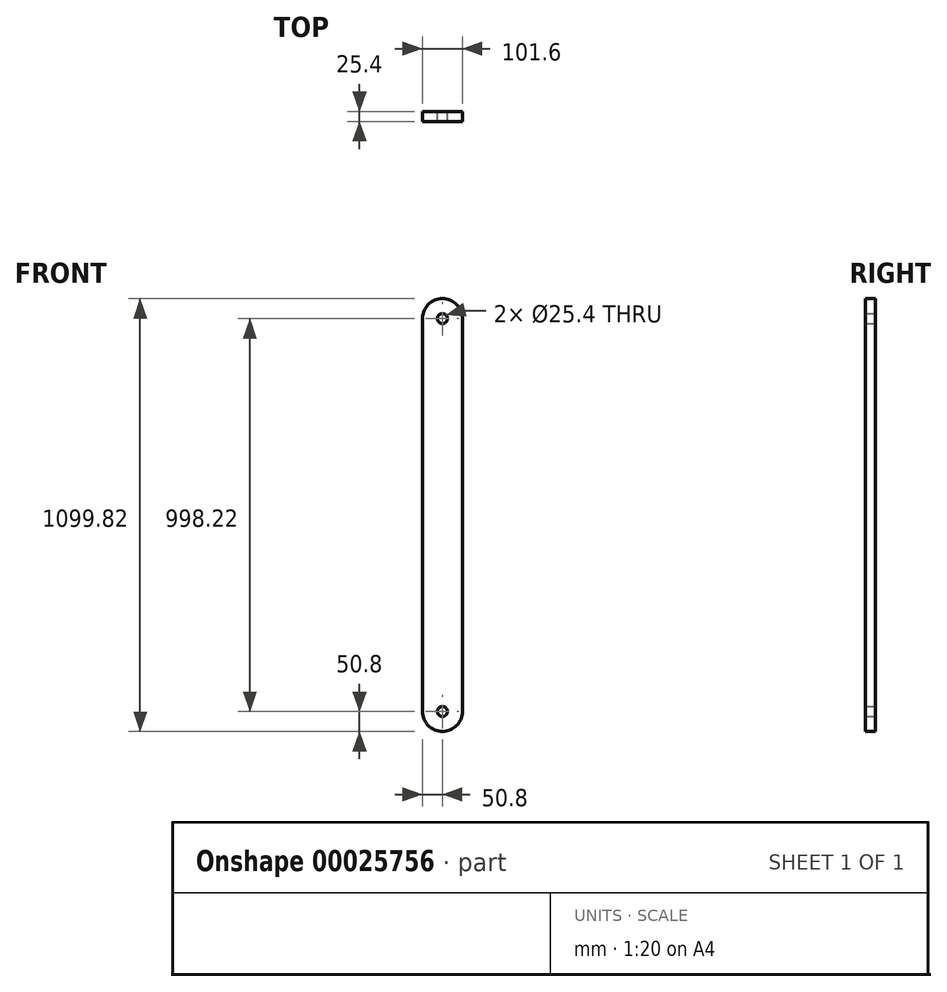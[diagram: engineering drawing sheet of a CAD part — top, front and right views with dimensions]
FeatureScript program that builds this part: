
annotation { "Feature Type Name" : "Feature", "Feature Type Description" : "" }
export const myFeature = defineFeature(function(context is Context, id is Id, definition is map)
    precondition{}
    {
        {
            var Q0;
            Q0=qCreatedBy(makeId("Front.planeOp"),FACE);
            var sketch = newSketch(context, id + "F0", { "sketchPlane" : qUnion([Q0])});
            skArc(sketch, "E0", {"start": v(-101.6, 0) * mm, "mid": v(-50.8, -50.8) * mm, "end": v(0, 0) * mm});
            skLineSegment(sketch, "E1", {"start": v(-101.6, 0) * mm, "end": v(-101.6, 998.22) * mm});
            skLineSegment(sketch, "E2", {"start": v(0, 0) * mm, "end": v(0, 998.22) * mm});
            skArc(sketch, "E3", {"start": v(0, 998.22) * mm, "mid": v(-50.8, 1049.02) * mm, "end": v(-101.6, 998.22) * mm});
            skCircle(sketch, "E4", {"center": v(-50.8, 998.22) * mm, "radius": 12.7 * mm});
            skCircle(sketch, "E5", {"center": v(-50.8, 0) * mm, "radius": 12.7 * mm});
            skSolve(sketch);
        }
        {
            var Q0;
            Q0 = qSketchRegion(id + "F0", true);
            extrude(context, id + "F1", {"entities" : qUnion([Q0]), "depth" : 25.4 * mm});
        }
    });
